# Revit family: ГРЕЕРС ЗВ - 150 В
name_source: partatom
category: Wyposażenie mechaniczne
revit_build: Autodesk Revit 2016 (Build: 20150220_1215(x64)
units: mm (PartAtom-declared; Revit-internal decimal feet)

## family parameters
Obiekt nadrzędny = Powierzchnia
Punkt obliczania pomieszczeń = Nie
Tnij formami wycięć po wczytaniu = Nie
Typ części = Normalny
Współdzielony = Nie
Wymiar okrągłego złącza = Użyj średnicy

## types (60) — shared parameters
Bec аппарата, наполненного водой = 30.00 kg
Domyślna rzędna = 2200 mm
IP = 21
Model = ГРЕЕРС ЗВ - 150 В
Opis = Воздушная завеса
Producent = ГРЕЕРС
Автор = www.archispace.com
Вентилятор = Однофазный двигатель с поперечным ротором
Вес аппарата = 27.50 kg
Данные продукта = https://greers.ru
Длина = 1500 mm  [stored 4.92126 ft]
Классификация нагрузки = ДВИГАТЕЛЬ
Коэффициент мощности = 0.96
Макс. потребление тока = 1 A
Материал = ГРЕЕРС-сталь-белый
Материал 2 = ГРЕЕРС-сталь,перфорация-белый
Напряжение питания = 230 V
Патрубки = 3/4"
Полная мощность = 219 VA

## per-type parameters (varying)
| type | Tемпература воды на выходе из теплообменника (Tw2) | Количество воды проходящей через теплообменник | Падение давления воды в теплообменнике | Производительность | Температура воды на входе в теплообменник (Tw1) | Температура воздуха на входе в аппарат (Тр1) | Температура воздуха на выходе из аппарата (Тр2) | Тепловая мощность |
| ГРЕЕРС ЗВ - 150 В, 1 скорость, Tw1/Tw2 = 90/70°C, Tp1 = 0 | 70 °C | 0.269 L/s | 16.6 kPa | 1600 m³/h | 90 °C | 0 °C | 40.5 °C | 21.9 kW |
| ГРЕЕРС ЗВ - 150 В, 1 скорость, Tw1/Tw2 = 90/70°C, Tp1 = 5 | 70 °C | 0.252 L/s | 14.8 kPa | 1600 m³/h | 90 °C | 5 °C | 43 °C | 20.6 kW |
| ГРЕЕРС ЗВ - 150 В, 1 скорость, Tw1/Tw2 = 90/70°C, Tp1 = 10 | 70 °C | 0.235 L/s | 13 kPa | 1600 m³/h | 90 °C | 10 °C | 45.5 °C | 19.2 kW |
| ГРЕЕРС ЗВ - 150 В, 1 скорость, Tw1/Tw2 = 90/70°C, Tp1 = 15 | 70 °C | 0.218 L/s | 11.4 kPa | 1600 m³/h | 90 °C | 15 °C | 47.5 °C | 17.8 kW |
| ГРЕЕРС ЗВ - 150 В, 1 скорость, Tw1/Tw2 = 90/70°C, Tp1 = 20 | 70 °C | 0.201 L/s | 9.8 kPa | 1600 m³/h | 90 °C | 20 °C | 50 °C | 16.4 kW |
| ГРЕЕРС ЗВ - 150 В, 1 скорость, Tw1/Tw2 = 80/60°C, Tp1 = 0 | 60 °C | 0.231 L/s | 13 kPa | 1600 m³/h | 80 °C | 0 °C | 35 °C | 18.9 kW |
| ГРЕЕРС ЗВ - 150 В, 1 скорость, Tw1/Tw2 = 80/60°C, Tp1 = 5 | 60 °C | 0.214 L/s | 11.3 kPa | 1600 m³/h | 80 °C | 5 °C | 37.5 °C | 17.6 kW |
| ГРЕЕРС ЗВ - 150 В, 1 скорость, Tw1/Tw2 = 80/60°C, Tp1 = 10 | 60 °C | 0.197 L/s | 9.8 kPa | 1600 m³/h | 80 °C | 10 °C | 40 °C | 16.2 kW |
| ГРЕЕРС ЗВ - 150 В, 1 скорость, Tw1/Tw2 = 80/60°C, Tp1 = 15 | 60 °C | 0.18 L/s | 8.3 kPa | 1600 m³/h | 80 °C | 15 °C | 42 °C | 14.8 kW |
| ГРЕЕРС ЗВ - 150 В, 1 скорость, Tw1/Tw2 = 80/60°C, Tp1 = 20 | 60 °C | 0.163 L/s | 6.9 kPa | 1600 m³/h | 80 °C | 20 °C | 44.5 °C | 13.4 kW |
| ГРЕЕРС ЗВ - 150 В, 1 скорость, Tw1/Tw2 = 70/50°C, Tp1 = 0 | 50 °C | 0.193 L/s | 9.7 kPa | 1600 m³/h | 70 °C | 0 °C | 29.5 °C | 15.9 kW |
| ГРЕЕРС ЗВ - 150 В, 1 скорость, Tw1/Tw2 = 70/50°C, Tp1 = 5 | 50 °C | 0.177 L/s | 8.3 kPa | 1600 m³/h | 70 °C | 5 °C | 32 °C | 14.5 kW |
| ГРЕЕРС ЗВ - 150 В, 1 скорость, Tw1/Tw2 = 70/50°C, Tp1 = 10 | 50 °C | 0.159 L/s | 6.9 kPa | 1600 m³/h | 70 °C | 10 °C | 34 °C | 13.1 kW |
| ГРЕЕРС ЗВ - 150 В, 1 скорость, Tw1/Tw2 = 70/50°C, Tp1 = 15 | 50 °C | 0.142 L/s | 5.6 kPa | 1600 m³/h | 70 °C | 15 °C | 36.5 °C | 11.7 kW |
| ГРЕЕРС ЗВ - 150 В, 1 скорость, Tw1/Tw2 = 70/50°C, Tp1 = 20 | 50 °C | 0.125 L/s | 4.5 kPa | 1600 m³/h | 70 °C | 20 °C | 39 °C | 10.3 kW |
| ГРЕЕРС ЗВ - 150 В, 1 скорость, Tw1/Tw2 = 60/40°C, Tp1 = 0 | 40 °C | 0.156 L/s | 6.9 kPa | 1600 m³/h | 60 °C | 0 °C | 24 °C | 12.9 kW |
| ГРЕЕРС ЗВ - 150 В, 1 скорость, Tw1/Tw2 = 60/40°C, Tp1 = 5 | 40 °C | 0.139 L/s | 5.6 kPa | 1600 m³/h | 60 °C | 5 °C | 26 °C | 11.5 kW |
| ГРЕЕРС ЗВ - 150 В, 1 скорость, Tw1/Tw2 = 60/40°C, Tp1 = 10 | 40 °C | 0.122 L/s | 4.4 kPa | 1600 m³/h | 60 °C | 10 °C | 28.5 °C | 10 kW |
| ГРЕЕРС ЗВ - 150 В, 1 скорость, Tw1/Tw2 = 60/40°C, Tp1 = 15 | 40 °C | 0.104 L/s | 3.4 kPa | 1600 m³/h | 60 °C | 15 °C | 31 °C | 8.6 kW |
| ГРЕЕРС ЗВ - 150 В, 1 скорость, Tw1/Tw2 = 60/40°C, Tp1 = 20 | 40 °C | 0.086 L/s | 2.4 kPa | 1600 m³/h | 60 °C | 20 °C | 33 °C | 7.1 kW |
| ГРЕЕРС ЗВ - 150 В, 2 скорость, Tw1/Tw2 = 90/70°C, Tp1 = 0 | 70 °C | 0.295 L/s | 19.6 kPa | 1850 m³/h | 90 °C | 0 °C | 38.5 °C | 24.1 kW |
| ГРЕЕРС ЗВ - 150 В, 2 скорость, Tw1/Tw2 = 90/70°C, Tp1 = 5 | 70 °C | 0.277 L/s | 17.5 kPa | 1850 m³/h | 90 °C | 5 °C | 41 °C | 22.6 kW |
| ГРЕЕРС ЗВ - 150 В, 2 скорость, Tw1/Tw2 = 90/70°C, Tp1 = 10 | 70 °C | 0.258 L/s | 15.4 kPa | 1850 m³/h | 90 °C | 10 °C | 43.5 °C | 21.1 kW |
| ГРЕЕРС ЗВ - 150 В, 2 скорость, Tw1/Tw2 = 90/70°C, Tp1 = 15 | 70 °C | 0.239 L/s | 13.4 kPa | 1850 m³/h | 90 °C | 15 °C | 46 °C | 19.5 kW |
| ГРЕЕРС ЗВ - 150 В, 2 скорость, Tw1/Tw2 = 90/70°C, Tp1 = 20 | 70 °C | 0.22 L/s | 11.6 kPa | 1850 m³/h | 90 °C | 20 °C | 48.5 °C | 18 kW |
| ГРЕЕРС ЗВ - 150 В, 2 скорость, Tw1/Tw2 = 80/60°C, Tp1 = 0 | 60 °C | 0.253 L/s | 15.3 kPa | 1850 m³/h | 80 °C | 0 °C | 33 °C | 20.8 kW |
| ГРЕЕРС ЗВ - 150 В, 2 скорость, Tw1/Tw2 = 80/60°C, Tp1 = 5 | 60 °C | 0.235 L/s | 13.4 kPa | 1850 m³/h | 80 °C | 5 °C | 35.5 °C | 19.3 kW |
| ГРЕЕРС ЗВ - 150 В, 2 скорость, Tw1/Tw2 = 80/60°C, Tp1 = 10 | 60 °C | 0.216 L/s | 11.5 kPa | 1850 m³/h | 80 °C | 10 °C | 38 °C | 17.7 kW |
| ГРЕЕРС ЗВ - 150 В, 2 скорость, Tw1/Tw2 = 80/60°C, Tp1 = 15 | 60 °C | 0.198 L/s | 9.8 kPa | 1850 m³/h | 80 °C | 15 °C | 40.5 °C | 16.2 kW |
| ГРЕЕРС ЗВ - 150 В, 2 скорость, Tw1/Tw2 = 80/60°C, Tp1 = 20 | 60 °C | 0.179 L/s | 8.2 kPa | 1850 m³/h | 80 °C | 20 °C | 43 °C | 14.6 kW |
| ГРЕЕРС ЗВ - 150 В, 2 скорость, Tw1/Tw2 = 70/50°C, Tp1 = 0 | 50 °C | 0.212 L/s | 11.5 kPa | 1850 m³/h | 70 °C | 0 °C | 28 °C | 17.5 kW |
| ГРЕЕРС ЗВ - 150 В, 2 скорость, Tw1/Tw2 = 70/50°C, Tp1 = 5 | 50 °C | 0.194 L/s | 9.8 kPa | 1850 m³/h | 70 °C | 5 °C | 30.5 °C | 15.9 kW |
| ГРЕЕРС ЗВ - 150 В, 2 скорость, Tw1/Tw2 = 70/50°C, Tp1 = 10 | 50 °C | 0.175 L/s | 8.1 kPa | 1850 m³/h | 70 °C | 10 °C | 33 °C | 14.4 kW |
| ГРЕЕРС ЗВ - 150 В, 2 скорость, Tw1/Tw2 = 70/50°C, Tp1 = 15 | 50 °C | 0.156 L/s | 6.6 kPa | 1850 m³/h | 70 °C | 15 °C | 35.5 °C | 12.8 kW |
| ГРЕЕРС ЗВ - 150 В, 2 скорость, Tw1/Tw2 = 70/50°C, Tp1 = 20 | 50 °C | 0.137 L/s | 5.2 kPa | 1850 m³/h | 70 °C | 20 °C | 38 °C | 11.3 kW |
| ГРЕЕРС ЗВ - 150 В, 2 скорость, Tw1/Tw2 = 60/40°C, Tp1 = 0 | 40 °C | 0.171 L/s | 8.1 kPa | 1850 m³/h | 60 °C | 0 °C | 22.5 °C | 14.1 kW |
| ГРЕЕРС ЗВ - 150 В, 2 скорость, Tw1/Tw2 = 60/40°C, Tp1 = 5 | 40 °C | 0.152 L/s | 6.6 kPa | 1850 m³/h | 60 °C | 5 °C | 25 °C | 12.6 kW |
| ГРЕЕРС ЗВ - 150 В, 2 скорость, Tw1/Tw2 = 60/40°C, Tp1 = 10 | 40 °C | 0.133 L/s | 5.2 kPa | 1850 m³/h | 60 °C | 10 °C | 27.5 °C | 11 kW |
| ГРЕЕРС ЗВ - 150 В, 2 скорость, Tw1/Tw2 = 60/40°C, Tp1 = 15 | 40 °C | 0.114 L/s | 4 kPa | 1850 m³/h | 60 °C | 15 °C | 30 °C | 9.4 kW |
| ГРЕЕРС ЗВ - 150 В, 2 скорость, Tw1/Tw2 = 60/40°C, Tp1 = 20 | 40 °C | 0.095 L/s | 2.8 kPa | 1850 m³/h | 60 °C | 20 °C | 32.5 °C | 7.8 kW |
| ГРЕЕРС ЗВ - 150 В, 3 скорость, Tw1/Tw2 = 90/70°C, Tp1 = 0 | 70 °C | 0.319 L/s | 22.7 kPa | 2100 m³/h | 90 °C | 0 °C | 36.5 °C | 26.1 kW |
| ГРЕЕРС ЗВ - 150 В, 3 скорость, Tw1/Tw2 = 90/70°C, Tp1 = 5 | 70 °C | 0.299 L/s | 20.2 kPa | 2100 m³/h | 90 °C | 5 °C | 39.5 °C | 24.4 kW |
| ГРЕЕРС ЗВ - 150 В, 3 скорость, Tw1/Tw2 = 90/70°C, Tp1 = 10 | 70 °C | 0.279 L/s | 17.8 kPa | 2100 m³/h | 90 °C | 10 °C | 42 °C | 22.8 kW |
| ГРЕЕРС ЗВ - 150 В, 3 скорость, Tw1/Tw2 = 90/70°C, Tp1 = 15 | 70 °C | 0.259 L/s | 15.5 kPa | 2100 m³/h | 90 °C | 15 °C | 44.5 °C | 21.1 kW |
| ГРЕЕРС ЗВ - 150 В, 3 скорость, Tw1/Tw2 = 90/70°C, Tp1 = 20 | 70 °C | 0.239 L/s | 13.4 kPa | 2100 m³/h | 90 °C | 20 °C | 47 °C | 19.5 kW |
| ГРЕЕРС ЗВ - 150 В, 3 скорость, Tw1/Tw2 = 80/60°C, Tp1 = 0 | 60 °C | 0.274 L/s | 17.7 kPa | 2100 m³/h | 80 °C | 0 °C | 31.5 °C | 22.5 kW |
| ГРЕЕРС ЗВ - 150 В, 3 скорость, Tw1/Tw2 = 80/60°C, Tp1 = 5 | 60 °C | 0.254 L/s | 15.4 kPa | 2100 m³/h | 80 °C | 5 °C | 34.5 °C | 20.8 kW |
| ГРЕЕРС ЗВ - 150 В, 3 скорость, Tw1/Tw2 = 80/60°C, Tp1 = 10 | 60 °C | 0.234 L/s | 13.3 kPa | 2100 m³/h | 80 °C | 10 °C | 37 °C | 19.2 kW |
| ГРЕЕРС ЗВ - 150 В, 3 скорость, Tw1/Tw2 = 80/60°C, Tp1 = 15 | 60 °C | 0.214 L/s | 11.3 kPa | 2100 m³/h | 80 °C | 15 °C | 39.5 °C | 17.5 kW |
| ГРЕЕРС ЗВ - 150 В, 3 скорость, Tw1/Tw2 = 80/60°C, Tp1 = 20 | 60 °C | 0.193 L/s | 9.4 kPa | 2100 m³/h | 80 °C | 20 °C | 42 °C | 15.8 kW |
| ГРЕЕРС ЗВ - 150 В, 3 скорость, Tw1/Tw2 = 70/50°C, Tp1 = 0 | 50 °C | 0.229 L/s | 13.2 kPa | 2100 m³/h | 70 °C | 0 °C | 26.5 °C | 18.9 kW |
| ГРЕЕРС ЗВ - 150 В, 3 скорость, Tw1/Tw2 = 70/50°C, Tp1 = 5 | 50 °C | 0.209 L/s | 11.2 kPa | 2100 m³/h | 70 °C | 5 °C | 29 °C | 17.2 kW |
| ГРЕЕРС ЗВ - 150 В, 3 скорость, Tw1/Tw2 = 70/50°C, Tp1 = 10 | 50 °C | 0.189 L/s | 9.4 kPa | 2100 m³/h | 70 °C | 10 °C | 32 °C | 15.6 kW |
| ГРЕЕРС ЗВ - 150 В, 3 скорость, Tw1/Tw2 = 70/50°C, Tp1 = 15 | 50 °C | 0.169 L/s | 7.6 kPa | 2100 m³/h | 70 °C | 15 °C | 34.5 °C | 13.9 kW |
| ГРЕЕРС ЗВ - 150 В, 3 скорость, Tw1/Tw2 = 70/50°C, Tp1 = 20 | 50 °C | 0.148 L/s | 6 kPa | 2100 m³/h | 70 °C | 20 °C | 37 °C | 12.2 kW |
| ГРЕЕРС ЗВ - 150 В, 3 скорость, Tw1/Tw2 = 60/40°C, Tp1 = 0 | 40 °C | 0.185 L/s | 9.3 kPa | 2100 m³/h | 60 °C | 0 °C | 21.5 °C | 15.3 kW |
| ГРЕЕРС ЗВ - 150 В, 3 скорость, Tw1/Tw2 = 60/40°C, Tp1 = 5 | 40 °C | 0.165 L/s | 7.6 kPa | 2100 m³/h | 60 °C | 5 °C | 24 °C | 13.6 kW |
| ГРЕЕРС ЗВ - 150 В, 3 скорость, Tw1/Tw2 = 60/40°C, Tp1 = 10 | 40 °C | 0.144 L/s | 6 kPa | 2100 m³/h | 60 °C | 10 °C | 26.5 °C | 11.9 kW |
| ГРЕЕРС ЗВ - 150 В, 3 скорость, Tw1/Tw2 = 60/40°C, Tp1 = 15 | 40 °C | 0.124 L/s | 4.5 kPa | 2100 m³/h | 60 °C | 15 °C | 29.5 °C | 10.2 kW |
| ГРЕЕРС ЗВ - 150 В, 3 скорость, Tw1/Tw2 = 60/40°C, Tp1 = 20 | 40 °C | 0.102 L/s | 3.3 kPa | 2100 m³/h | 60 °C | 20 °C | 32 °C | 8.5 kW |

note: [stored X ft] marks values corroborated as IEEE doubles in the binary element streams (Revit-internal decimal feet)
